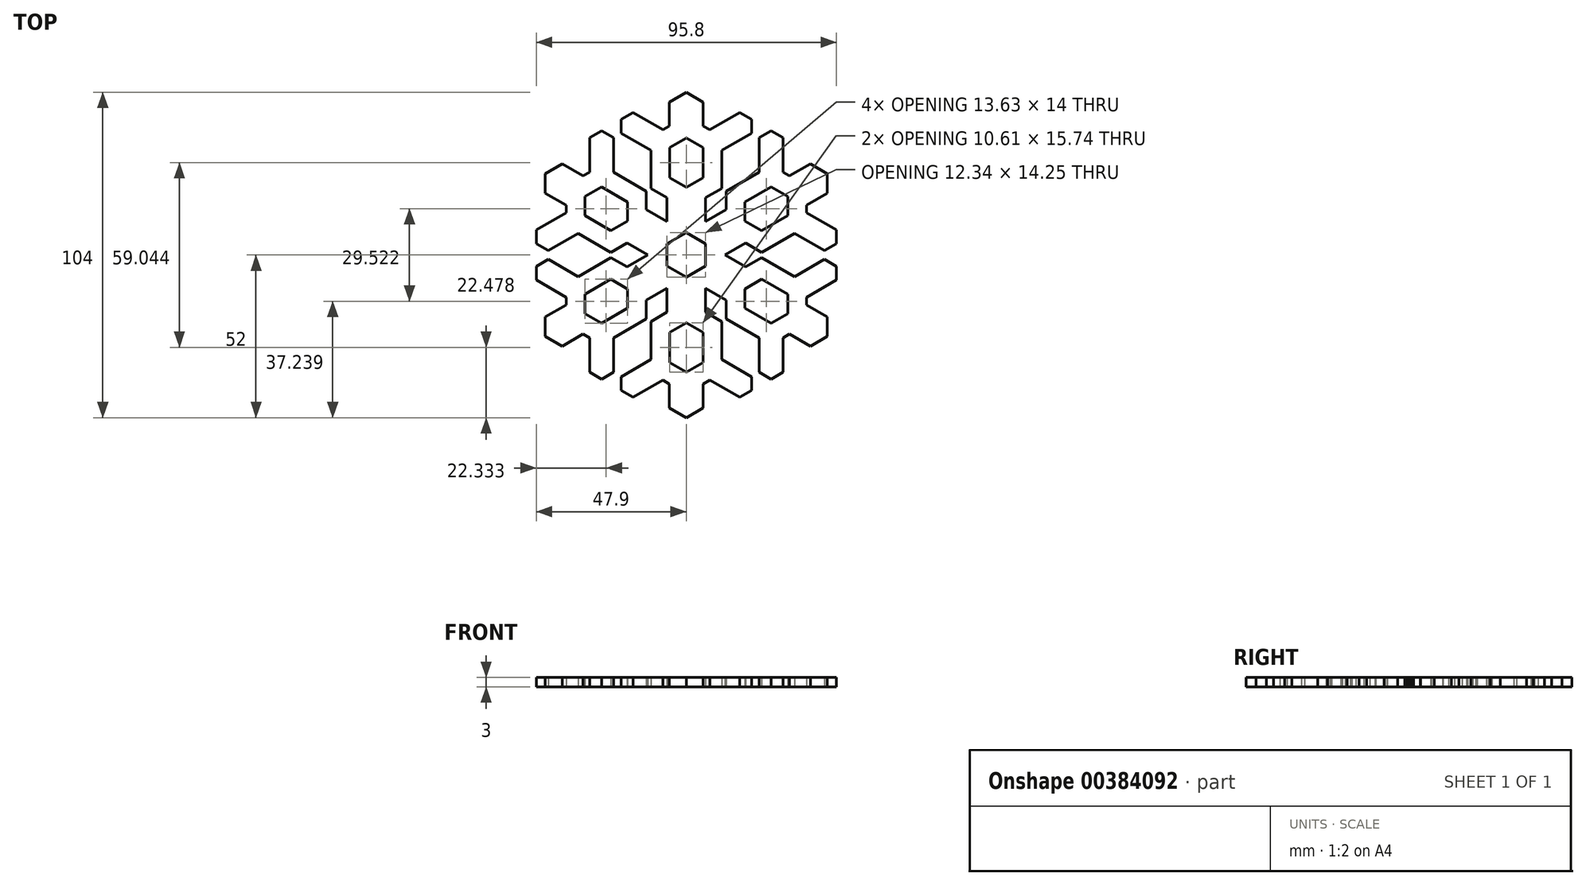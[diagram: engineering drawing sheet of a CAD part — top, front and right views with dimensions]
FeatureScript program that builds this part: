
annotation { "Feature Type Name" : "Feature", "Feature Type Description" : "" }
export const myFeature = defineFeature(function(context is Context, id is Id, definition is map)
    precondition{}
    {
        {
            var Q0;
            Q0=qCreatedBy(makeId("Top.planeOp"),FACE);
            var sketch = newSketch(context, id + "F0", { "sketchPlane" : qUnion([Q0])});
            skLineSegment(sketch, "E0", {"start": v(0, 26) * mm, "end": v(0, -26) * mm, "construction": true});
            skLineSegment(sketch, "E1", {"start": v(22.52, -13) * mm, "end": v(-22.52, 13) * mm, "construction": true});
            skLineSegment(sketch, "E2", {"start": v(-22.52, -13) * mm, "end": v(22.52, 13) * mm, "construction": true});
            skLineSegment(sketch, "E3", {"start": v(-3.08, 1.78) * mm, "end": v(-3.08, 9.14) * mm});
            skLineSegment(sketch, "E4", {"start": v(-3.08, 9.14) * mm, "end": v(-5.65, 10.63) * mm});
            skLineSegment(sketch, "E5", {"start": v(-5.65, 10.63) * mm, "end": v(-5.65, 18.9) * mm});
            skLineSegment(sketch, "E6", {"start": v(-5.65, 18.9) * mm, "end": v(0, 22.16) * mm});
            skLineSegment(sketch, "E7", {"start": v(0, 26) * mm, "end": v(-2.71, 24.44) * mm});
            skLineSegment(sketch, "E8", {"start": v(-2.71, 24.44) * mm, "end": v(-2.71, 20.6) * mm});
            skLineSegment(sketch, "E9", {"start": v(-3.75, 20) * mm, "end": v(-8.5, 22.74) * mm});
            skLineSegment(sketch, "E10", {"start": v(-8.5, 22.74) * mm, "end": v(-10.41, 21.64) * mm});
            skLineSegment(sketch, "E11", {"start": v(-10.41, 21.64) * mm, "end": v(-10.41, 19.44) * mm});
            skLineSegment(sketch, "E12", {"start": v(-10.41, 19.44) * mm, "end": v(-5.65, 16.7) * mm});
            skLineSegment(sketch, "E13", {"start": v(-10.41, 19.44) * mm, "end": v(-8.5, 22.74) * mm, "construction": true});
            skPoint(sketch, "E14", {"position": v(-9.46, 21.1) * mm});
            skLineSegment(sketch, "E15", {"start": v(-10.41, 21.64) * mm, "end": v(-5.65, 18.9) * mm, "construction": true});
            skLineSegment(sketch, "E16.MirrorCS", {"start": v(10.41, 21.64) * mm, "end": v(10.41, 19.44) * mm});
            skLineSegment(sketch, "E17.MirrorCS", {"start": v(10.41, 21.64) * mm, "end": v(5.65, 18.9) * mm, "construction": true});
            skPoint(sketch, "E18.MirrorP", {"position": v(9.46, 21.1) * mm});
            skLineSegment(sketch, "E19.MirrorCS", {"start": v(10.41, 19.44) * mm, "end": v(8.5, 22.74) * mm, "construction": true});
            skLineSegment(sketch, "E20.MirrorCS", {"start": v(10.41, 19.44) * mm, "end": v(5.65, 16.7) * mm});
            skLineSegment(sketch, "E21.MirrorCS", {"start": v(3.08, 1.78) * mm, "end": v(3.08, 9.14) * mm});
            skLineSegment(sketch, "E22.MirrorCS", {"start": v(0, 26) * mm, "end": v(2.71, 24.44) * mm});
            skLineSegment(sketch, "E23.MirrorCS", {"start": v(3.08, 9.14) * mm, "end": v(5.65, 10.63) * mm});
            skLineSegment(sketch, "E24.MirrorCS", {"start": v(3.75, 20) * mm, "end": v(8.5, 22.74) * mm});
            skLineSegment(sketch, "E25.MirrorCS", {"start": v(2.71, 24.44) * mm, "end": v(2.71, 20.6) * mm});
            skLineSegment(sketch, "E26.MirrorCS", {"start": v(5.65, 10.63) * mm, "end": v(5.65, 18.9) * mm});
            skLineSegment(sketch, "E27.MirrorCS", {"start": v(8.5, 22.74) * mm, "end": v(10.41, 21.64) * mm});
            skLineSegment(sketch, "E28.MirrorCS", {"start": v(5.65, 18.9) * mm, "end": v(0, 22.16) * mm});
            skLineSegment(sketch, "E29", {"start": v(0, 18.7) * mm, "end": v(-2.65, 17.16) * mm});
            skLineSegment(sketch, "E30", {"start": v(-2.65, 17.16) * mm, "end": v(-2.65, 12.36) * mm});
            skLineSegment(sketch, "E31", {"start": v(-2.65, 12.36) * mm, "end": v(0, 10.83) * mm});
            skLineSegment(sketch, "E32.MirrorCS", {"start": v(0, 18.7) * mm, "end": v(2.65, 17.16) * mm});
            skLineSegment(sketch, "E33.MirrorCS", {"start": v(2.65, 17.16) * mm, "end": v(2.65, 12.36) * mm});
            skLineSegment(sketch, "E34.MirrorCS", {"start": v(2.65, 12.36) * mm, "end": v(0, 10.83) * mm});
            skLineSegment(sketch, "E35.1.0", {"start": v(-22.52, 9.87) * mm, "end": v(-19.2, 7.95) * mm});
            skLineSegment(sketch, "E35.1.1", {"start": v(-22.04, 0.7) * mm, "end": v(-17.29, 3.45) * mm});
            skLineSegment(sketch, "E35.1.2", {"start": v(-22.52, 13) * mm, "end": v(-22.52, 9.87) * mm});
            skLineSegment(sketch, "E35.1.3", {"start": v(-23.95, 4) * mm, "end": v(-23.95, 1.8) * mm});
            skLineSegment(sketch, "E35.1.4", {"start": v(-19.2, 6.75) * mm, "end": v(-23.95, 4) * mm});
            skLineSegment(sketch, "E35.1.5", {"start": v(-19.2, 4.55) * mm, "end": v(-19.2, 11.08) * mm});
            skLineSegment(sketch, "E35.1.6", {"start": v(-16.2, 9.35) * mm, "end": v(-16.2, 6.28) * mm});
            skLineSegment(sketch, "E35.1.7", {"start": v(-15.44, 13.24) * mm, "end": v(-15.44, 18.74) * mm});
            skLineSegment(sketch, "E35.1.8", {"start": v(-15.44, 18.74) * mm, "end": v(-13.54, 19.84) * mm});
            skLineSegment(sketch, "E35.1.9", {"start": v(-19.8, 14.56) * mm, "end": v(-16.48, 12.64) * mm});
            skLineSegment(sketch, "E35.1.10", {"start": v(-12.03, 0.42) * mm, "end": v(-19.2, 4.55) * mm});
            skLineSegment(sketch, "E35.1.11", {"start": v(-13.54, 10.88) * mm, "end": v(-9.38, 8.48) * mm});
            skLineSegment(sketch, "E35.1.12", {"start": v(-9.46, 1.9) * mm, "end": v(-12.03, 0.42) * mm});
            skLineSegment(sketch, "E35.1.13", {"start": v(-3.08, -1.78) * mm, "end": v(-9.46, 1.9) * mm});
            skLineSegment(sketch, "E35.1.14", {"start": v(-22.52, 13) * mm, "end": v(-19.8, 14.56) * mm});
            skPoint(sketch, "E35.1.15", {"position": v(-23, 2.35) * mm});
            skLineSegment(sketch, "E35.1.16", {"start": v(-23.95, 1.8) * mm, "end": v(-19.2, 4.55) * mm, "construction": true});
            skLineSegment(sketch, "E35.1.17", {"start": v(0, 3.56) * mm, "end": v(-6.38, 7.24) * mm});
            skLineSegment(sketch, "E35.1.18", {"start": v(-16.2, 9.35) * mm, "end": v(-13.54, 10.88) * mm});
            skLineSegment(sketch, "E35.1.19", {"start": v(-6.38, 7.24) * mm, "end": v(-6.38, 10.2) * mm});
            skLineSegment(sketch, "E35.1.20", {"start": v(-6.38, 10.2) * mm, "end": v(-13.54, 14.34) * mm});
            skLineSegment(sketch, "E35.1.21", {"start": v(-13.54, 14.34) * mm, "end": v(-19.2, 11.08) * mm});
            skLineSegment(sketch, "E35.1.22", {"start": v(-16.2, 6.28) * mm, "end": v(-12.03, 3.88) * mm});
            skPoint(sketch, "E35.1.23", {"position": v(-13.54, 18.74) * mm});
            skLineSegment(sketch, "E35.1.24", {"start": v(-12.03, 3.88) * mm, "end": v(-9.38, 5.41) * mm});
            skLineSegment(sketch, "E35.1.25", {"start": v(-11.63, 18.74) * mm, "end": v(-11.63, 13.24) * mm});
            skLineSegment(sketch, "E35.1.26", {"start": v(-13.54, 19.84) * mm, "end": v(-13.54, 14.34) * mm, "construction": true});
            skLineSegment(sketch, "E35.1.27", {"start": v(-9.38, 8.48) * mm, "end": v(-9.38, 5.41) * mm});
            skLineSegment(sketch, "E35.1.28", {"start": v(-23.95, 1.8) * mm, "end": v(-22.04, 0.7) * mm});
            skLineSegment(sketch, "E35.1.29", {"start": v(-13.54, 19.84) * mm, "end": v(-11.63, 18.74) * mm});
            skLineSegment(sketch, "E35.1.30", {"start": v(-11.63, 18.74) * mm, "end": v(-15.44, 18.74) * mm, "construction": true});
            skLineSegment(sketch, "E35.1.31", {"start": v(-22.04, 0.7) * mm, "end": v(-23.95, 4) * mm, "construction": true});
            skLineSegment(sketch, "E35.2.0", {"start": v(-19.8, -14.56) * mm, "end": v(-16.48, -12.64) * mm});
            skLineSegment(sketch, "E35.2.1", {"start": v(-11.63, -18.74) * mm, "end": v(-11.63, -13.24) * mm});
            skLineSegment(sketch, "E35.2.2", {"start": v(-22.52, -13) * mm, "end": v(-19.8, -14.56) * mm});
            skLineSegment(sketch, "E35.2.3", {"start": v(-15.44, -18.74) * mm, "end": v(-13.54, -19.84) * mm});
            skLineSegment(sketch, "E35.2.4", {"start": v(-15.44, -13.24) * mm, "end": v(-15.44, -18.74) * mm});
            skLineSegment(sketch, "E35.2.5", {"start": v(-13.54, -14.34) * mm, "end": v(-19.2, -11.08) * mm});
            skLineSegment(sketch, "E35.2.6", {"start": v(-16.2, -9.35) * mm, "end": v(-13.54, -10.88) * mm});
            skLineSegment(sketch, "E35.2.7", {"start": v(-19.2, -6.75) * mm, "end": v(-23.95, -4) * mm});
            skLineSegment(sketch, "E35.2.8", {"start": v(-23.95, -4) * mm, "end": v(-23.95, -1.8) * mm});
            skLineSegment(sketch, "E35.2.9", {"start": v(-22.52, -9.87) * mm, "end": v(-19.2, -7.95) * mm});
            skLineSegment(sketch, "E35.2.10", {"start": v(-6.38, -10.2) * mm, "end": v(-13.54, -14.34) * mm});
            skLineSegment(sketch, "E35.2.11", {"start": v(-16.2, -6.28) * mm, "end": v(-12.03, -3.88) * mm});
            skLineSegment(sketch, "E35.2.12", {"start": v(-6.38, -7.24) * mm, "end": v(-6.38, -10.2) * mm});
            skLineSegment(sketch, "E35.2.13", {"start": v(0, -3.56) * mm, "end": v(-6.38, -7.24) * mm});
            skLineSegment(sketch, "E35.2.14", {"start": v(-22.52, -13) * mm, "end": v(-22.52, -9.87) * mm});
            skPoint(sketch, "E35.2.15", {"position": v(-13.54, -18.74) * mm});
            skLineSegment(sketch, "E35.2.16", {"start": v(-13.54, -19.84) * mm, "end": v(-13.54, -14.34) * mm, "construction": true});
            skLineSegment(sketch, "E35.2.17", {"start": v(-3.08, 1.78) * mm, "end": v(-9.46, -1.9) * mm});
            skLineSegment(sketch, "E35.2.18", {"start": v(-16.2, -9.35) * mm, "end": v(-16.2, -6.28) * mm});
            skLineSegment(sketch, "E35.2.19", {"start": v(-9.46, -1.9) * mm, "end": v(-12.03, -0.42) * mm});
            skLineSegment(sketch, "E35.2.20", {"start": v(-12.03, -0.42) * mm, "end": v(-19.2, -4.55) * mm});
            skLineSegment(sketch, "E35.2.21", {"start": v(-19.2, -4.55) * mm, "end": v(-19.2, -11.08) * mm});
            skLineSegment(sketch, "E35.2.22", {"start": v(-13.54, -10.88) * mm, "end": v(-9.38, -8.48) * mm});
            skPoint(sketch, "E35.2.23", {"position": v(-23, -2.35) * mm});
            skLineSegment(sketch, "E35.2.24", {"start": v(-9.38, -8.48) * mm, "end": v(-9.38, -5.41) * mm});
            skLineSegment(sketch, "E35.2.25", {"start": v(-22.04, -0.7) * mm, "end": v(-17.29, -3.45) * mm});
            skLineSegment(sketch, "E35.2.26", {"start": v(-23.95, -1.8) * mm, "end": v(-19.2, -4.55) * mm, "construction": true});
            skLineSegment(sketch, "E35.2.27", {"start": v(-12.03, -3.88) * mm, "end": v(-9.38, -5.41) * mm});
            skLineSegment(sketch, "E35.2.28", {"start": v(-13.54, -19.84) * mm, "end": v(-11.63, -18.74) * mm});
            skLineSegment(sketch, "E35.2.29", {"start": v(-23.95, -1.8) * mm, "end": v(-22.04, -0.7) * mm});
            skLineSegment(sketch, "E35.2.30", {"start": v(-22.04, -0.7) * mm, "end": v(-23.95, -4) * mm, "construction": true});
            skLineSegment(sketch, "E35.2.31", {"start": v(-11.63, -18.74) * mm, "end": v(-15.44, -18.74) * mm, "construction": true});
            skLineSegment(sketch, "E35.3.0", {"start": v(2.71, -24.44) * mm, "end": v(2.71, -20.6) * mm});
            skLineSegment(sketch, "E35.3.1", {"start": v(10.41, -19.44) * mm, "end": v(5.65, -16.7) * mm});
            skLineSegment(sketch, "E35.3.2", {"start": v(0, -26) * mm, "end": v(2.71, -24.44) * mm});
            skLineSegment(sketch, "E35.3.3", {"start": v(8.5, -22.74) * mm, "end": v(10.41, -21.64) * mm});
            skLineSegment(sketch, "E35.3.4", {"start": v(3.75, -20) * mm, "end": v(8.5, -22.74) * mm});
            skLineSegment(sketch, "E35.3.5", {"start": v(5.65, -18.9) * mm, "end": v(0, -22.16) * mm});
            skLineSegment(sketch, "E35.3.6", {"start": v(0, -18.7) * mm, "end": v(2.65, -17.16) * mm});
            skLineSegment(sketch, "E35.3.7", {"start": v(-3.75, -20) * mm, "end": v(-8.5, -22.74) * mm});
            skLineSegment(sketch, "E35.3.8", {"start": v(-8.5, -22.74) * mm, "end": v(-10.41, -21.64) * mm});
            skLineSegment(sketch, "E35.3.9", {"start": v(-2.71, -24.44) * mm, "end": v(-2.71, -20.6) * mm});
            skLineSegment(sketch, "E35.3.10", {"start": v(5.65, -10.63) * mm, "end": v(5.65, -18.9) * mm});
            skLineSegment(sketch, "E35.3.11", {"start": v(-2.65, -17.16) * mm, "end": v(-2.65, -12.36) * mm});
            skLineSegment(sketch, "E35.3.12", {"start": v(3.08, -9.14) * mm, "end": v(5.65, -10.63) * mm});
            skLineSegment(sketch, "E35.3.13", {"start": v(3.08, -1.78) * mm, "end": v(3.08, -9.14) * mm});
            skLineSegment(sketch, "E35.3.14", {"start": v(0, -26) * mm, "end": v(-2.71, -24.44) * mm});
            skPoint(sketch, "E35.3.15", {"position": v(9.46, -21.1) * mm});
            skLineSegment(sketch, "E35.3.16", {"start": v(10.41, -21.64) * mm, "end": v(5.65, -18.9) * mm, "construction": true});
            skLineSegment(sketch, "E35.3.17", {"start": v(-3.08, -1.78) * mm, "end": v(-3.08, -9.14) * mm});
            skLineSegment(sketch, "E35.3.18", {"start": v(0, -18.7) * mm, "end": v(-2.65, -17.16) * mm});
            skLineSegment(sketch, "E35.3.19", {"start": v(-3.08, -9.14) * mm, "end": v(-5.65, -10.63) * mm});
            skLineSegment(sketch, "E35.3.20", {"start": v(-5.65, -10.63) * mm, "end": v(-5.65, -18.9) * mm});
            skLineSegment(sketch, "E35.3.21", {"start": v(-5.65, -18.9) * mm, "end": v(0, -22.16) * mm});
            skLineSegment(sketch, "E35.3.22", {"start": v(2.65, -17.16) * mm, "end": v(2.65, -12.36) * mm});
            skPoint(sketch, "E35.3.23", {"position": v(-9.46, -21.1) * mm});
            skLineSegment(sketch, "E35.3.24", {"start": v(2.65, -12.36) * mm, "end": v(0, -10.83) * mm});
            skLineSegment(sketch, "E35.3.25", {"start": v(-10.41, -19.44) * mm, "end": v(-5.65, -16.7) * mm});
            skLineSegment(sketch, "E35.3.26", {"start": v(-10.41, -21.64) * mm, "end": v(-5.65, -18.9) * mm, "construction": true});
            skLineSegment(sketch, "E35.3.27", {"start": v(-2.65, -12.36) * mm, "end": v(0, -10.83) * mm});
            skLineSegment(sketch, "E35.3.28", {"start": v(10.41, -21.64) * mm, "end": v(10.41, -19.44) * mm});
            skLineSegment(sketch, "E35.3.29", {"start": v(-10.41, -21.64) * mm, "end": v(-10.41, -19.44) * mm});
            skLineSegment(sketch, "E35.3.30", {"start": v(-10.41, -19.44) * mm, "end": v(-8.5, -22.74) * mm, "construction": true});
            skLineSegment(sketch, "E35.3.31", {"start": v(10.41, -19.44) * mm, "end": v(8.5, -22.74) * mm, "construction": true});
            skLineSegment(sketch, "E35.4.0", {"start": v(22.52, -9.87) * mm, "end": v(19.2, -7.95) * mm});
            skLineSegment(sketch, "E35.4.1", {"start": v(22.04, -0.7) * mm, "end": v(17.29, -3.45) * mm});
            skLineSegment(sketch, "E35.4.2", {"start": v(22.52, -13) * mm, "end": v(22.52, -9.87) * mm});
            skLineSegment(sketch, "E35.4.3", {"start": v(23.95, -4) * mm, "end": v(23.95, -1.8) * mm});
            skLineSegment(sketch, "E35.4.4", {"start": v(19.2, -6.75) * mm, "end": v(23.95, -4) * mm});
            skLineSegment(sketch, "E35.4.5", {"start": v(19.2, -4.55) * mm, "end": v(19.2, -11.08) * mm});
            skLineSegment(sketch, "E35.4.6", {"start": v(16.2, -9.35) * mm, "end": v(16.2, -6.28) * mm});
            skLineSegment(sketch, "E35.4.7", {"start": v(15.44, -13.24) * mm, "end": v(15.44, -18.74) * mm});
            skLineSegment(sketch, "E35.4.8", {"start": v(15.44, -18.74) * mm, "end": v(13.54, -19.84) * mm});
            skLineSegment(sketch, "E35.4.9", {"start": v(19.8, -14.56) * mm, "end": v(16.48, -12.64) * mm});
            skLineSegment(sketch, "E35.4.10", {"start": v(12.03, -0.42) * mm, "end": v(19.2, -4.55) * mm});
            skLineSegment(sketch, "E35.4.11", {"start": v(13.54, -10.88) * mm, "end": v(9.38, -8.48) * mm});
            skLineSegment(sketch, "E35.4.12", {"start": v(9.46, -1.9) * mm, "end": v(12.03, -0.42) * mm});
            skLineSegment(sketch, "E35.4.13", {"start": v(3.08, 1.78) * mm, "end": v(9.46, -1.9) * mm});
            skLineSegment(sketch, "E35.4.14", {"start": v(22.52, -13) * mm, "end": v(19.8, -14.56) * mm});
            skPoint(sketch, "E35.4.15", {"position": v(23, -2.35) * mm});
            skLineSegment(sketch, "E35.4.16", {"start": v(23.95, -1.8) * mm, "end": v(19.2, -4.55) * mm, "construction": true});
            skLineSegment(sketch, "E35.4.17", {"start": v(0, -3.56) * mm, "end": v(6.38, -7.24) * mm});
            skLineSegment(sketch, "E35.4.18", {"start": v(16.2, -9.35) * mm, "end": v(13.54, -10.88) * mm});
            skLineSegment(sketch, "E35.4.19", {"start": v(6.38, -7.24) * mm, "end": v(6.38, -10.2) * mm});
            skLineSegment(sketch, "E35.4.20", {"start": v(6.38, -10.2) * mm, "end": v(13.54, -14.34) * mm});
            skLineSegment(sketch, "E35.4.21", {"start": v(13.54, -14.34) * mm, "end": v(19.2, -11.08) * mm});
            skLineSegment(sketch, "E35.4.22", {"start": v(16.2, -6.28) * mm, "end": v(12.03, -3.88) * mm});
            skPoint(sketch, "E35.4.23", {"position": v(13.54, -18.74) * mm});
            skLineSegment(sketch, "E35.4.24", {"start": v(12.03, -3.88) * mm, "end": v(9.38, -5.41) * mm});
            skLineSegment(sketch, "E35.4.25", {"start": v(11.63, -18.74) * mm, "end": v(11.63, -13.24) * mm});
            skLineSegment(sketch, "E35.4.26", {"start": v(13.54, -19.84) * mm, "end": v(13.54, -14.34) * mm, "construction": true});
            skLineSegment(sketch, "E35.4.27", {"start": v(9.38, -8.48) * mm, "end": v(9.38, -5.41) * mm});
            skLineSegment(sketch, "E35.4.28", {"start": v(23.95, -1.8) * mm, "end": v(22.04, -0.7) * mm});
            skLineSegment(sketch, "E35.4.29", {"start": v(13.54, -19.84) * mm, "end": v(11.63, -18.74) * mm});
            skLineSegment(sketch, "E35.4.30", {"start": v(11.63, -18.74) * mm, "end": v(15.44, -18.74) * mm, "construction": true});
            skLineSegment(sketch, "E35.4.31", {"start": v(22.04, -0.7) * mm, "end": v(23.95, -4) * mm, "construction": true});
            skLineSegment(sketch, "E35.5.0", {"start": v(19.8, 14.56) * mm, "end": v(16.48, 12.64) * mm});
            skLineSegment(sketch, "E35.5.1", {"start": v(11.63, 18.74) * mm, "end": v(11.63, 13.24) * mm});
            skLineSegment(sketch, "E35.5.2", {"start": v(22.52, 13) * mm, "end": v(19.8, 14.56) * mm});
            skLineSegment(sketch, "E35.5.3", {"start": v(15.44, 18.74) * mm, "end": v(13.54, 19.84) * mm});
            skLineSegment(sketch, "E35.5.4", {"start": v(15.44, 13.24) * mm, "end": v(15.44, 18.74) * mm});
            skLineSegment(sketch, "E35.5.5", {"start": v(13.54, 14.34) * mm, "end": v(19.2, 11.08) * mm});
            skLineSegment(sketch, "E35.5.6", {"start": v(16.2, 9.35) * mm, "end": v(13.54, 10.88) * mm});
            skLineSegment(sketch, "E35.5.7", {"start": v(19.2, 6.75) * mm, "end": v(23.95, 4) * mm});
            skLineSegment(sketch, "E35.5.8", {"start": v(23.95, 4) * mm, "end": v(23.95, 1.8) * mm});
            skLineSegment(sketch, "E35.5.9", {"start": v(22.52, 9.87) * mm, "end": v(19.2, 7.95) * mm});
            skLineSegment(sketch, "E35.5.10", {"start": v(6.38, 10.2) * mm, "end": v(13.54, 14.34) * mm});
            skLineSegment(sketch, "E35.5.11", {"start": v(16.2, 6.28) * mm, "end": v(12.03, 3.88) * mm});
            skLineSegment(sketch, "E35.5.12", {"start": v(6.38, 7.24) * mm, "end": v(6.38, 10.2) * mm});
            skLineSegment(sketch, "E35.5.13", {"start": v(0, 3.56) * mm, "end": v(6.38, 7.24) * mm});
            skLineSegment(sketch, "E35.5.14", {"start": v(22.52, 13) * mm, "end": v(22.52, 9.87) * mm});
            skPoint(sketch, "E35.5.15", {"position": v(13.54, 18.74) * mm});
            skLineSegment(sketch, "E35.5.16", {"start": v(13.54, 19.84) * mm, "end": v(13.54, 14.34) * mm, "construction": true});
            skLineSegment(sketch, "E35.5.17", {"start": v(3.08, -1.78) * mm, "end": v(9.46, 1.9) * mm});
            skLineSegment(sketch, "E35.5.18", {"start": v(16.2, 9.35) * mm, "end": v(16.2, 6.28) * mm});
            skLineSegment(sketch, "E35.5.19", {"start": v(9.46, 1.9) * mm, "end": v(12.03, 0.42) * mm});
            skLineSegment(sketch, "E35.5.20", {"start": v(12.03, 0.42) * mm, "end": v(19.2, 4.55) * mm});
            skLineSegment(sketch, "E35.5.21", {"start": v(19.2, 4.55) * mm, "end": v(19.2, 11.08) * mm});
            skLineSegment(sketch, "E35.5.22", {"start": v(13.54, 10.88) * mm, "end": v(9.38, 8.48) * mm});
            skPoint(sketch, "E35.5.23", {"position": v(23, 2.35) * mm});
            skLineSegment(sketch, "E35.5.24", {"start": v(9.38, 8.48) * mm, "end": v(9.38, 5.41) * mm});
            skLineSegment(sketch, "E35.5.25", {"start": v(22.04, 0.7) * mm, "end": v(17.29, 3.45) * mm});
            skLineSegment(sketch, "E35.5.26", {"start": v(23.95, 1.8) * mm, "end": v(19.2, 4.55) * mm, "construction": true});
            skLineSegment(sketch, "E35.5.27", {"start": v(12.03, 3.88) * mm, "end": v(9.38, 5.41) * mm});
            skLineSegment(sketch, "E35.5.28", {"start": v(13.54, 19.84) * mm, "end": v(11.63, 18.74) * mm});
            skLineSegment(sketch, "E35.5.29", {"start": v(23.95, 1.8) * mm, "end": v(22.04, 0.7) * mm});
            skLineSegment(sketch, "E35.5.30", {"start": v(22.04, 0.7) * mm, "end": v(23.95, 4) * mm, "construction": true});
            skLineSegment(sketch, "E35.5.31", {"start": v(11.63, 18.74) * mm, "end": v(15.44, 18.74) * mm, "construction": true});
            skPoint(sketch, "E35.center", {"position": v(0, 0) * mm});
            skLineSegment(sketch, "E36", {"start": v(-3.08, 1.78) * mm, "end": v(0, 3.56) * mm});
            skLineSegment(sketch, "E37", {"start": v(3.08, 1.78) * mm, "end": v(3.08, -1.78) * mm});
            skLineSegment(sketch, "E38", {"start": v(3.08, -1.78) * mm, "end": v(0, -3.56) * mm});
            skLineSegment(sketch, "E39", {"start": v(0, -3.56) * mm, "end": v(-3.08, -1.78) * mm});
            skLineSegment(sketch, "E40", {"start": v(-3.08, -1.78) * mm, "end": v(-3.08, 1.78) * mm});
            skLineSegment(sketch, "E41", {"start": v(0, 3.56) * mm, "end": v(3.08, 1.78) * mm});
            skSolve(sketch);
        }
        {
            var Q0;
            Q0 = qSketchRegion(id + "F0", true);
            extrude(context, id + "F1", {"entities" : qUnion([Q0]), "depth" : 1.5 * mm});
        }
        {
            var Q0;
            Q0=makeQuery(id+"F1.opExtrude","SWEPT_BODY",BODY,{"disambiguationData":[OSD([sQuery(id+"F0.wireOp",EDGE,"E3"),sQuery(id+"F0.wireOp",EDGE,"E4"),sQuery(id+"F0.wireOp",EDGE,"E5"),sQuery(id+"F0.wireOp",EDGE,"E6"),sQuery(id+"F0.wireOp",EDGE,"E7"),sQuery(id+"F0.wireOp",EDGE,"E8"),sQuery(id+"F0.wireOp",EDGE,"E9"),sQuery(id+"F0.wireOp",EDGE,"E10"),sQuery(id+"F0.wireOp",EDGE,"E11"),sQuery(id+"F0.wireOp",EDGE,"E12"),sQuery(id+"F0.wireOp",EDGE,"E16.MirrorCS"),sQuery(id+"F0.wireOp",EDGE,"E20.MirrorCS"),sQuery(id+"F0.wireOp",EDGE,"E21.MirrorCS"),sQuery(id+"F0.wireOp",EDGE,"E22.MirrorCS"),sQuery(id+"F0.wireOp",EDGE,"E23.MirrorCS"),sQuery(id+"F0.wireOp",EDGE,"E24.MirrorCS"),sQuery(id+"F0.wireOp",EDGE,"E25.MirrorCS"),sQuery(id+"F0.wireOp",EDGE,"E26.MirrorCS"),sQuery(id+"F0.wireOp",EDGE,"E27.MirrorCS"),sQuery(id+"F0.wireOp",EDGE,"E28.MirrorCS"),sQuery(id+"F0.wireOp",EDGE,"E29"),sQuery(id+"F0.wireOp",EDGE,"E30"),sQuery(id+"F0.wireOp",EDGE,"E31"),sQuery(id+"F0.wireOp",EDGE,"E32.MirrorCS"),sQuery(id+"F0.wireOp",EDGE,"E33.MirrorCS"),sQuery(id+"F0.wireOp",EDGE,"E34.MirrorCS"),sQuery(id+"F0.wireOp",EDGE,"E35.1.0"),sQuery(id+"F0.wireOp",EDGE,"E35.1.1"),sQuery(id+"F0.wireOp",EDGE,"E35.1.2"),sQuery(id+"F0.wireOp",EDGE,"E35.1.3"),sQuery(id+"F0.wireOp",EDGE,"E35.1.4"),sQuery(id+"F0.wireOp",EDGE,"E35.1.5"),sQuery(id+"F0.wireOp",EDGE,"E35.1.6"),sQuery(id+"F0.wireOp",EDGE,"E35.1.7"),sQuery(id+"F0.wireOp",EDGE,"E35.1.8"),sQuery(id+"F0.wireOp",EDGE,"E35.1.9"),sQuery(id+"F0.wireOp",EDGE,"E35.1.10"),sQuery(id+"F0.wireOp",EDGE,"E35.1.11"),sQuery(id+"F0.wireOp",EDGE,"E35.1.12"),sQuery(id+"F0.wireOp",EDGE,"E35.1.13"),sQuery(id+"F0.wireOp",EDGE,"E35.1.14"),sQuery(id+"F0.wireOp",EDGE,"E35.1.17"),sQuery(id+"F0.wireOp",EDGE,"E35.1.18"),sQuery(id+"F0.wireOp",EDGE,"E35.1.19"),sQuery(id+"F0.wireOp",EDGE,"E35.1.20"),sQuery(id+"F0.wireOp",EDGE,"E35.1.21"),sQuery(id+"F0.wireOp",EDGE,"E35.1.22"),sQuery(id+"F0.wireOp",EDGE,"E35.1.24"),sQuery(id+"F0.wireOp",EDGE,"E35.1.25"),sQuery(id+"F0.wireOp",EDGE,"E35.1.27"),sQuery(id+"F0.wireOp",EDGE,"E35.1.28"),sQuery(id+"F0.wireOp",EDGE,"E35.1.29"),sQuery(id+"F0.wireOp",EDGE,"E35.2.0"),sQuery(id+"F0.wireOp",EDGE,"E35.2.1"),sQuery(id+"F0.wireOp",EDGE,"E35.2.2"),sQuery(id+"F0.wireOp",EDGE,"E35.2.3"),sQuery(id+"F0.wireOp",EDGE,"E35.2.4"),sQuery(id+"F0.wireOp",EDGE,"E35.2.5"),sQuery(id+"F0.wireOp",EDGE,"E35.2.6"),sQuery(id+"F0.wireOp",EDGE,"E35.2.7"),sQuery(id+"F0.wireOp",EDGE,"E35.2.8"),sQuery(id+"F0.wireOp",EDGE,"E35.2.9"),sQuery(id+"F0.wireOp",EDGE,"E35.2.10"),sQuery(id+"F0.wireOp",EDGE,"E35.2.11"),sQuery(id+"F0.wireOp",EDGE,"E35.2.12"),sQuery(id+"F0.wireOp",EDGE,"E35.2.13"),sQuery(id+"F0.wireOp",EDGE,"E35.2.14"),sQuery(id+"F0.wireOp",EDGE,"E35.2.17"),sQuery(id+"F0.wireOp",EDGE,"E35.2.18"),sQuery(id+"F0.wireOp",EDGE,"E35.2.19"),sQuery(id+"F0.wireOp",EDGE,"E35.2.20"),sQuery(id+"F0.wireOp",EDGE,"E35.2.21"),sQuery(id+"F0.wireOp",EDGE,"E35.2.22"),sQuery(id+"F0.wireOp",EDGE,"E35.2.24"),sQuery(id+"F0.wireOp",EDGE,"E35.2.25"),sQuery(id+"F0.wireOp",EDGE,"E35.2.27"),sQuery(id+"F0.wireOp",EDGE,"E35.2.28"),sQuery(id+"F0.wireOp",EDGE,"E35.2.29"),sQuery(id+"F0.wireOp",EDGE,"E35.3.0"),sQuery(id+"F0.wireOp",EDGE,"E35.3.1"),sQuery(id+"F0.wireOp",EDGE,"E35.3.2"),sQuery(id+"F0.wireOp",EDGE,"E35.3.3"),sQuery(id+"F0.wireOp",EDGE,"E35.3.4"),sQuery(id+"F0.wireOp",EDGE,"E35.3.5"),sQuery(id+"F0.wireOp",EDGE,"E35.3.6"),sQuery(id+"F0.wireOp",EDGE,"E35.3.7"),sQuery(id+"F0.wireOp",EDGE,"E35.3.8"),sQuery(id+"F0.wireOp",EDGE,"E35.3.9"),sQuery(id+"F0.wireOp",EDGE,"E35.3.10"),sQuery(id+"F0.wireOp",EDGE,"E35.3.11"),sQuery(id+"F0.wireOp",EDGE,"E35.3.12"),sQuery(id+"F0.wireOp",EDGE,"E35.3.13"),sQuery(id+"F0.wireOp",EDGE,"E35.3.14"),sQuery(id+"F0.wireOp",EDGE,"E35.3.17"),sQuery(id+"F0.wireOp",EDGE,"E35.3.18"),sQuery(id+"F0.wireOp",EDGE,"E35.3.19"),sQuery(id+"F0.wireOp",EDGE,"E35.3.20"),sQuery(id+"F0.wireOp",EDGE,"E35.3.21"),sQuery(id+"F0.wireOp",EDGE,"E35.3.22"),sQuery(id+"F0.wireOp",EDGE,"E35.3.24"),sQuery(id+"F0.wireOp",EDGE,"E35.3.25"),sQuery(id+"F0.wireOp",EDGE,"E35.3.27"),sQuery(id+"F0.wireOp",EDGE,"E35.3.28"),sQuery(id+"F0.wireOp",EDGE,"E35.3.29"),sQuery(id+"F0.wireOp",EDGE,"E35.4.0"),sQuery(id+"F0.wireOp",EDGE,"E35.4.1"),sQuery(id+"F0.wireOp",EDGE,"E35.4.2"),sQuery(id+"F0.wireOp",EDGE,"E35.4.3"),sQuery(id+"F0.wireOp",EDGE,"E35.4.4"),sQuery(id+"F0.wireOp",EDGE,"E35.4.5"),sQuery(id+"F0.wireOp",EDGE,"E35.4.6"),sQuery(id+"F0.wireOp",EDGE,"E35.4.7"),sQuery(id+"F0.wireOp",EDGE,"E35.4.8"),sQuery(id+"F0.wireOp",EDGE,"E35.4.9"),sQuery(id+"F0.wireOp",EDGE,"E35.4.10"),sQuery(id+"F0.wireOp",EDGE,"E35.4.11"),sQuery(id+"F0.wireOp",EDGE,"E35.4.12"),sQuery(id+"F0.wireOp",EDGE,"E35.4.13"),sQuery(id+"F0.wireOp",EDGE,"E35.4.14"),sQuery(id+"F0.wireOp",EDGE,"E35.4.17"),sQuery(id+"F0.wireOp",EDGE,"E35.4.18"),sQuery(id+"F0.wireOp",EDGE,"E35.4.19"),sQuery(id+"F0.wireOp",EDGE,"E35.4.20"),sQuery(id+"F0.wireOp",EDGE,"E35.4.21"),sQuery(id+"F0.wireOp",EDGE,"E35.4.22"),sQuery(id+"F0.wireOp",EDGE,"E35.4.24"),sQuery(id+"F0.wireOp",EDGE,"E35.4.25"),sQuery(id+"F0.wireOp",EDGE,"E35.4.27"),sQuery(id+"F0.wireOp",EDGE,"E35.4.28"),sQuery(id+"F0.wireOp",EDGE,"E35.4.29"),sQuery(id+"F0.wireOp",EDGE,"E35.5.0"),sQuery(id+"F0.wireOp",EDGE,"E35.5.1"),sQuery(id+"F0.wireOp",EDGE,"E35.5.2"),sQuery(id+"F0.wireOp",EDGE,"E35.5.3"),sQuery(id+"F0.wireOp",EDGE,"E35.5.4"),sQuery(id+"F0.wireOp",EDGE,"E35.5.5"),sQuery(id+"F0.wireOp",EDGE,"E35.5.6"),sQuery(id+"F0.wireOp",EDGE,"E35.5.7"),sQuery(id+"F0.wireOp",EDGE,"E35.5.8"),sQuery(id+"F0.wireOp",EDGE,"E35.5.9"),sQuery(id+"F0.wireOp",EDGE,"E35.5.10"),sQuery(id+"F0.wireOp",EDGE,"E35.5.11"),sQuery(id+"F0.wireOp",EDGE,"E35.5.12"),sQuery(id+"F0.wireOp",EDGE,"E35.5.13"),sQuery(id+"F0.wireOp",EDGE,"E35.5.14"),sQuery(id+"F0.wireOp",EDGE,"E35.5.17"),sQuery(id+"F0.wireOp",EDGE,"E35.5.18"),sQuery(id+"F0.wireOp",EDGE,"E35.5.19"),sQuery(id+"F0.wireOp",EDGE,"E35.5.20"),sQuery(id+"F0.wireOp",EDGE,"E35.5.21"),sQuery(id+"F0.wireOp",EDGE,"E35.5.22"),sQuery(id+"F0.wireOp",EDGE,"E35.5.24"),sQuery(id+"F0.wireOp",EDGE,"E35.5.25"),sQuery(id+"F0.wireOp",EDGE,"E35.5.27"),sQuery(id+"F0.wireOp",EDGE,"E35.5.28"),sQuery(id+"F0.wireOp",EDGE,"E35.5.29"),sQuery(id+"F0.wireOp",EDGE,"E36"),sQuery(id+"F0.wireOp",EDGE,"E37"),sQuery(id+"F0.wireOp",EDGE,"E38"),sQuery(id+"F0.wireOp",EDGE,"E39"),sQuery(id+"F0.wireOp",EDGE,"E40"),sQuery(id+"F0.wireOp",EDGE,"E41")])]});
            var Q1;
            Q1=qCreatedBy(makeId("Origin.pointOp"),VERTEX);
            transform(context, id + "F2", {"entities" : qUnion([Q0]), "transformType" : TransformType.SCALE_UNIFORMLY, "scale" : 2, "scalePoint" : qUnion([Q1]), "makeCopy" : false});
        }
    });
